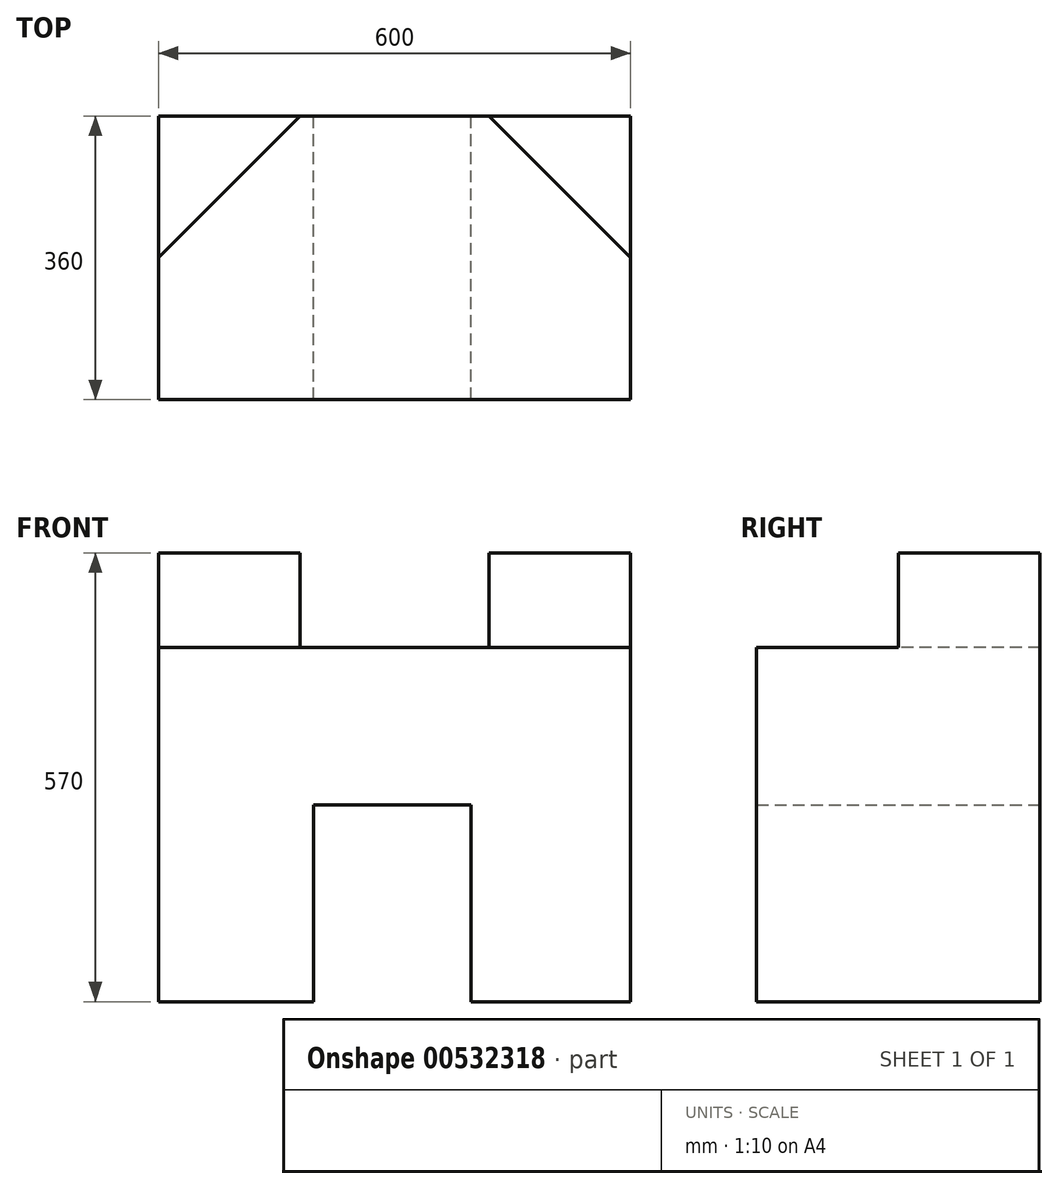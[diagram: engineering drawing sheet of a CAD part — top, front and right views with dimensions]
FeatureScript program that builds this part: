
annotation { "Feature Type Name" : "Feature", "Feature Type Description" : "" }
export const myFeature = defineFeature(function(context is Context, id is Id, definition is map)
    precondition{}
    {
        {
            var Q0;
            Q0=qCreatedBy(makeId("Front.planeOp"),FACE);
            var sketch = newSketch(context, id + "F0", { "sketchPlane" : qUnion([Q0])});
            skLineSegment(sketch, "E0.bottom", {"start": v(-297.1, 9.71) * mm, "end": v(302.9, 9.71) * mm});
            skLineSegment(sketch, "E0.top", {"start": v(-297.1, -440.29) * mm, "end": v(-100, -440.29) * mm});
            skLineSegment(sketch, "E0.left", {"start": v(-297.1, 9.71) * mm, "end": v(-297.1, -440.29) * mm});
            skLineSegment(sketch, "E0.right", {"start": v(302.9, 9.71) * mm, "end": v(302.9, -440.29) * mm});
            skPoint(sketch, "E1.end.orphan", {"position": v(114.7, -440.29) * mm});
            skLineSegment(sketch, "E2.bottom", {"start": v(100, -190.29) * mm, "end": v(-100, -190.29) * mm});
            skLineSegment(sketch, "E2.left", {"start": v(100, -190.29) * mm, "end": v(100, -440.29) * mm});
            skLineSegment(sketch, "E2.right", {"start": v(-100, -190.29) * mm, "end": v(-100, -440.29) * mm});
            skPoint(sketch, "E2.middle", {"position": v(0, -440.29) * mm});
            skPoint(sketch, "E2.top.end.orphan", {"position": v(-100, -690.29) * mm});
            skPoint(sketch, "E2.top.start.orphan", {"position": v(100, -690.29) * mm});
            skLineSegment(sketch, "E3.trimOffspring", {"start": v(100, -440.29) * mm, "end": v(302.9, -440.29) * mm});
            skSolve(sketch);
        }
        {
            var Q0;
            Q0 = qSketchRegion(id + "F0", true);
            extrude(context, id + "F1", {"entities" : qUnion([Q0]), "depth" : 360 * mm, "offsetDistance" : 25.4 * mm});
        }
        {
            var Q0;
            Q0=makeQuery(id+"F1.opExtrude","SWEPT_FACE",FACE,{"disambiguationData":[OSD([sQuery(id+"F0.wireOp",EDGE,"E0.bottom")])]});
            var sketch = newSketch(context, id + "F2", { "sketchPlane" : qUnion([Q0])});
            skLineSegment(sketch, "E4", {"start": v(-117.1, 0) * mm, "end": v(-297.1, -180) * mm});
            skLineSegment(sketch, "E5", {"start": v(122.9, 0) * mm, "end": v(302.9, -180) * mm});
            skSolve(sketch);
        }
        {
            var Q0;
            Q0 = qSketchRegion(id + "F2", true);
            var Q1;
            {var subQ0=sQuery(id+"F2.wireOp",EDGE,"E4");Q1=makeQuery(id+"F2.imprint","IMPRINT",FACE,{"disambiguationData":[TD([[makeQuery(id+"F2.imprint","IMPRINT",EDGE,{"derivedFrom":subQ0}),-1.0]])]});}
            var Q2;
            {var subQ0=sQuery(id+"F2.wireOp",EDGE,"E5");Q2=makeQuery(id+"F2.imprint","IMPRINT",FACE,{"disambiguationData":[TD([[makeQuery(id+"F2.imprint","IMPRINT",EDGE,{"derivedFrom":subQ0}),1.0]])]});}
            extrude(context, id + "F3", {"entities" : qUnion([Q0, Q1, Q2]), "operationType" : NewBodyOperationType.ADD, "depth" : 120 * mm, "offsetDistance" : 25.4 * mm});
        }
    });
